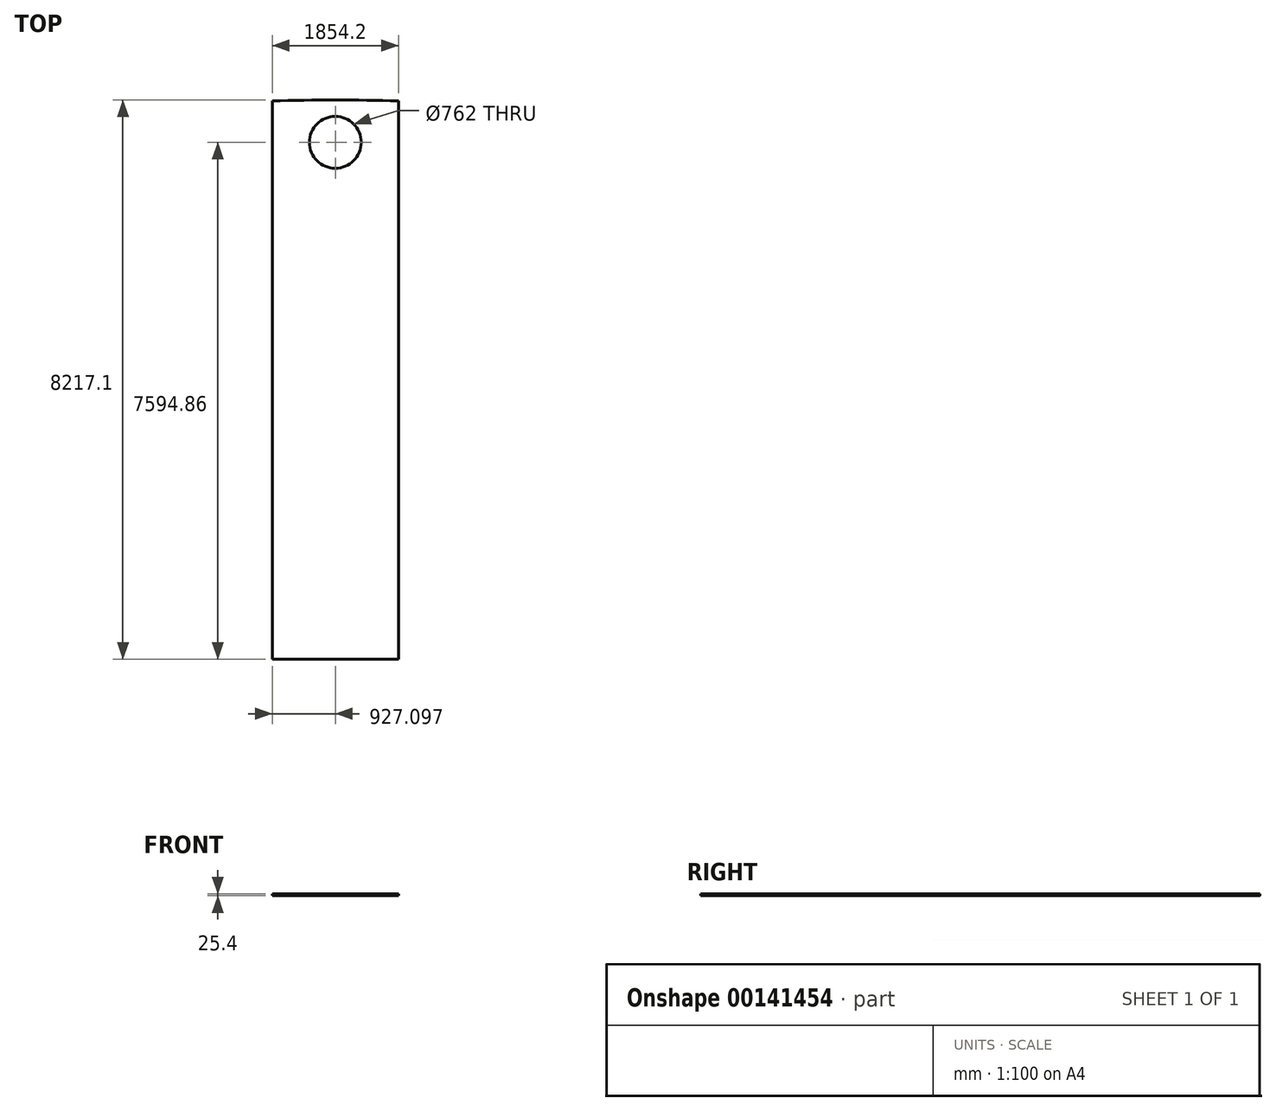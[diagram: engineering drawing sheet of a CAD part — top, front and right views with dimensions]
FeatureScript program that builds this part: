
annotation { "Feature Type Name" : "Feature", "Feature Type Description" : "" }
export const myFeature = defineFeature(function(context is Context, id is Id, definition is map)
    precondition{}
    {
        {
            var Q0;
            Q0=qCreatedBy(makeId("Top.planeOp"),FACE);
            var sketch = newSketch(context, id + "F0", { "sketchPlane" : qUnion([Q0])});
            skLineSegment(sketch, "E0", {"start": v(-8110.34, 0) * mm, "end": v(-6256.14, 0) * mm});
            skLineSegment(sketch, "E1", {"start": v(-6256.14, 0) * mm, "end": v(-6256.14, 8203.57) * mm});
            skLineSegment(sketch, "E2", {"start": v(-8110.34, 0) * mm, "end": v(-8110.34, 8203.57) * mm});
            skLineSegment(sketch, "E3", {"start": v(-7183.24, 0) * mm, "end": v(-7183.24, 8217.1) * mm});
            skArc(sketch, "E4", {"start": v(-6256.14, 8203.57) * mm, "mid": v(-7183.24, 8217.1) * mm, "end": v(-8110.34, 8203.57) * mm});
            skCircle(sketch, "E5", {"center": v(-7183.24, 7594.86) * mm, "radius": 381 * mm});
            skSolve(sketch);
        }
        {
            var Q0;
            {var subQ8=sQuery(id+"F0.wireOp",EDGE,"E2");Q0=makeQuery(id+"F0.imprint","IMPRINT",FACE,{"disambiguationData":[TD([[makeQuery(id+"F0.imprint","IMPRINT",EDGE,{"derivedFrom":subQ8}),-1.0]])]});}
            var Q1;
            {var subQ8=sQuery(id+"F0.wireOp",EDGE,"E1");Q1=makeQuery(id+"F0.imprint","IMPRINT",FACE,{"disambiguationData":[TD([[makeQuery(id+"F0.imprint","IMPRINT",EDGE,{"derivedFrom":subQ8}),1.0]])]});}
            extrude(context, id + "F1", {"entities" : qUnion([Q0, Q1]), "depth" : 25.4 * mm});
        }
    });
